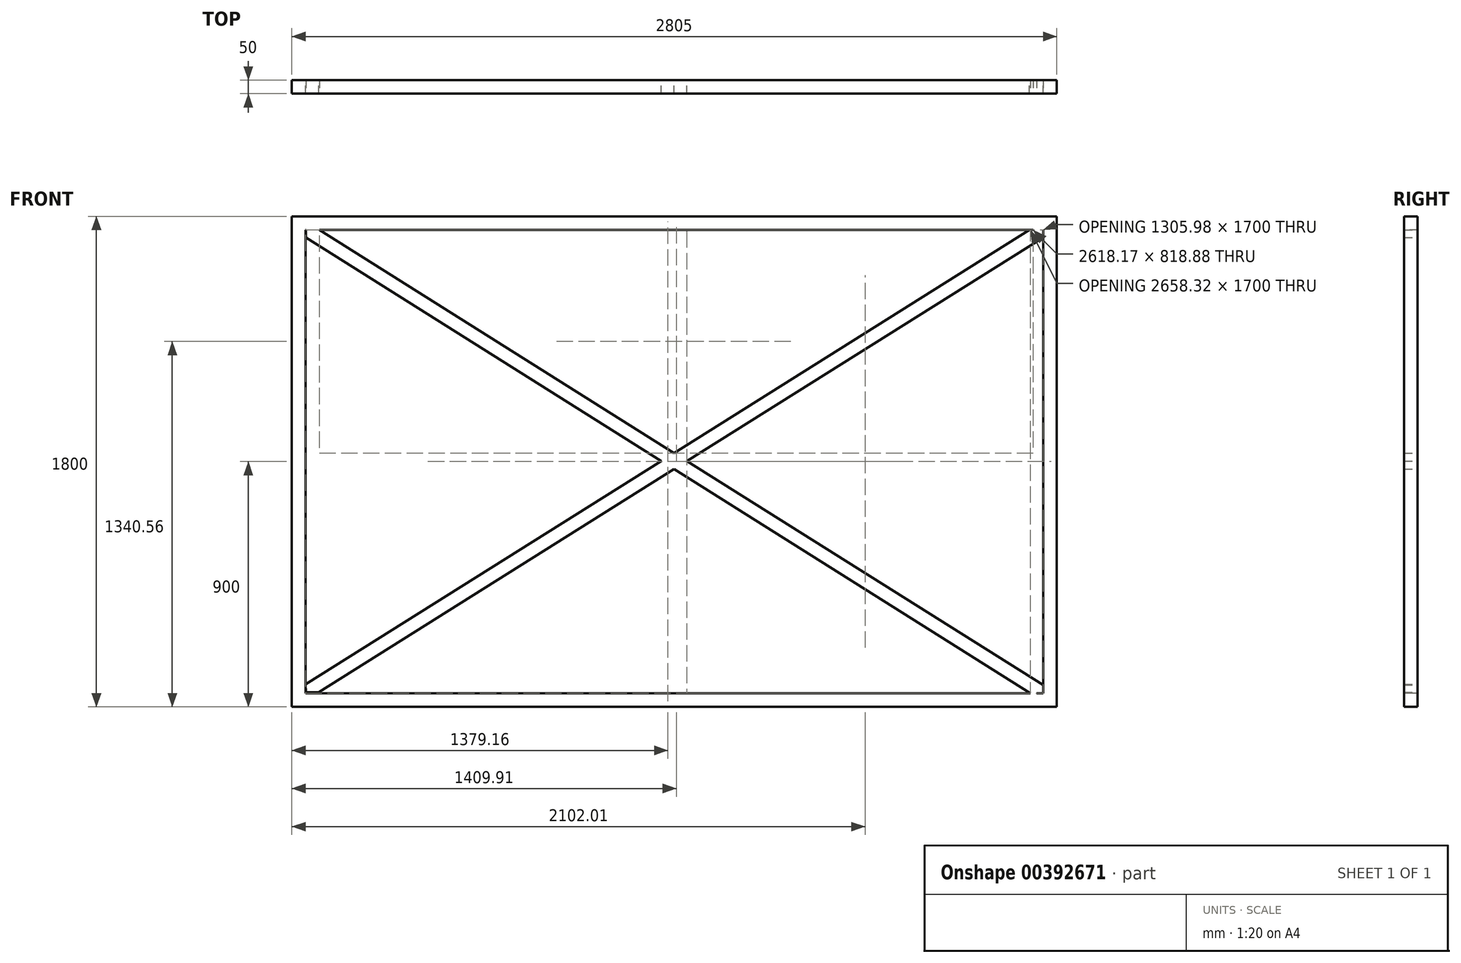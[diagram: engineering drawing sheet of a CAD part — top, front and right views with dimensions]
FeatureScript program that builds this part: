
annotation { "Feature Type Name" : "Feature", "Feature Type Description" : "" }
export const myFeature = defineFeature(function(context is Context, id is Id, definition is map)
    precondition{}
    {
        {
            var Q0;
            Q0=qCreatedBy(makeId("Front.planeOp"),FACE);
            var sketch = newSketch(context, id + "F0", { "sketchPlane" : qUnion([Q0])});
            skLineSegment(sketch, "E0.bottom", {"start": v(-1402.5, -900) * mm, "end": v(1402.5, -900) * mm});
            skLineSegment(sketch, "E0.top", {"start": v(-1402.5, 900) * mm, "end": v(1402.5, 900) * mm});
            skLineSegment(sketch, "E0.left", {"start": v(-1402.5, -900) * mm, "end": v(-1402.5, 900) * mm});
            skLineSegment(sketch, "E0.right", {"start": v(1402.5, -900) * mm, "end": v(1402.5, 900) * mm});
            skPoint(sketch, "E0.middle", {"position": v(0, 0) * mm});
            skLineSegment(sketch, "E1.bottom", {"start": v(-1352.5, -850) * mm, "end": v(1352.5, -850) * mm});
            skLineSegment(sketch, "E1.top", {"start": v(-1352.5, 850) * mm, "end": v(1352.5, 850) * mm});
            skLineSegment(sketch, "E1.left", {"start": v(-1352.5, -850) * mm, "end": v(-1352.5, 850) * mm});
            skLineSegment(sketch, "E1.right", {"start": v(1352.5, -850) * mm, "end": v(1352.5, 850) * mm});
            skSolve(sketch);
        }
        {
            var Q0;
            Q0 = qSketchRegion(id + "F0", true);
            extrude(context, id + "F1", {"entities" : qUnion([Q0]), "depth" : 50 * mm});
        }
        {
            var Q0;
            Q0=qCreatedBy(makeId("Front.planeOp"),FACE);
            var sketch = newSketch(context, id + "F2", { "sketchPlane" : qUnion([Q0])});
            skLineSegment(sketch, "E2", {"start": v(856.68, -567.35) * mm, "end": v(-1351.08, 822.02) * mm});
            skLineSegment(sketch, "E3", {"start": v(-1351.08, 822.02) * mm, "end": v(-1351.08, 851.56) * mm});
            skLineSegment(sketch, "E4", {"start": v(1027.56, -615.8) * mm, "end": v(-1302.44, 850.48) * mm});
            skLineSegment(sketch, "E5", {"start": v(-1302.44, 850.48) * mm, "end": v(-1351.08, 851.56) * mm});
            skLineSegment(sketch, "E6", {"start": v(-1351.08, 822.02) * mm, "end": v(1306.28, -850.29) * mm});
            skLineSegment(sketch, "E7", {"start": v(1306.28, -850.29) * mm, "end": v(1352.25, -849.68) * mm});
            skLineSegment(sketch, "E8", {"start": v(-1302.44, 850.48) * mm, "end": v(1352.25, -820.14) * mm});
            skLineSegment(sketch, "E9", {"start": v(1352.25, -820.14) * mm, "end": v(1352.25, -849.68) * mm});
            skLineSegment(sketch, "E10", {"start": v(1004.84, 603.74) * mm, "end": v(1352.23, 822.02) * mm});
            skLineSegment(sketch, "E11", {"start": v(1352.23, 822.02) * mm, "end": v(1352.25, 851.56) * mm});
            skLineSegment(sketch, "E12", {"start": v(904.97, 600.03) * mm, "end": v(1301.76, 849.36) * mm});
            skLineSegment(sketch, "E13", {"start": v(1301.76, 849.36) * mm, "end": v(1352.25, 851.56) * mm});
            skLineSegment(sketch, "E14", {"start": v(904.97, 600.03) * mm, "end": v(-1351.98, -818.13) * mm});
            skLineSegment(sketch, "E15", {"start": v(-1351.98, -818.13) * mm, "end": v(-1351.08, -847.1) * mm});
            skLineSegment(sketch, "E16", {"start": v(1004.84, 603.74) * mm, "end": v(-1304.1, -847.1) * mm});
            skLineSegment(sketch, "E17", {"start": v(-1304.1, -847.1) * mm, "end": v(-1351.08, -847.1) * mm});
            skSolve(sketch);
        }
        {
            var Q0;
            Q0 = qSketchRegion(id + "F2", true);
            extrude(context, id + "F3", {"entities" : qUnion([Q0]), "operationType" : NewBodyOperationType.ADD, "depth" : 50 * mm});
        }
    });
